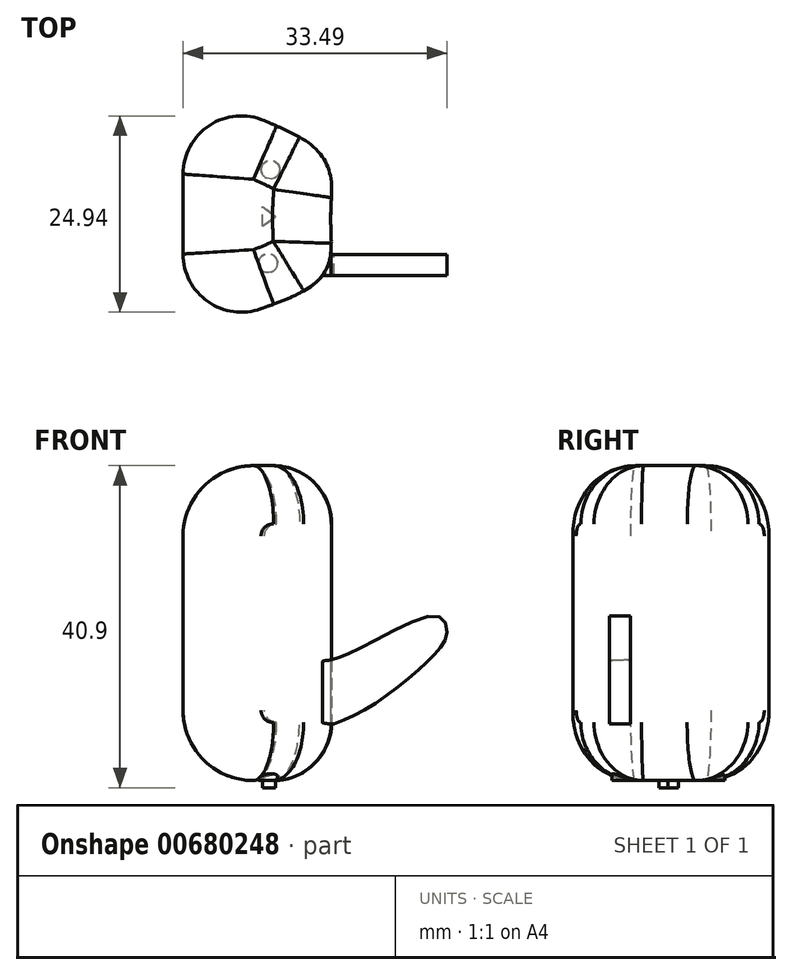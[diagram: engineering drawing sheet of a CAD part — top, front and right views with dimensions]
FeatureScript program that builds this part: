
annotation { "Feature Type Name" : "Feature", "Feature Type Description" : "" }
export const myFeature = defineFeature(function(context is Context, id is Id, definition is map)
    precondition{}
    {
        {
            var Q0;
            Q0=qCreatedBy(makeId("Top.planeOp"),FACE);
            var sketch = newSketch(context, id + "F0", { "sketchPlane" : qUnion([Q0])});
            skLineSegment(sketch, "E0", {"start": v(-0.87, 0) * mm, "end": v(-0.87, 30) * mm});
            skFitSpline(sketch, "E1", {"points": [v(-0.87, 0) * mm, v(9.33, 2.9) * mm, v(17.04, 7.3) * mm, v(17.87, 14.2) * mm, v(17.87, 19.53) * mm, v(15.67, 23.38) * mm, v(10.06, 26.42) * mm, v(4.27, 28.9) * mm, v(-0.87, 30) * mm], "startDerivative": vector(97.67, 19.37) * mm, "endDerivative": vector(-53.84, -1.92) * mm});
            skSolve(sketch);
        }
        {
            var Q0;
            Q0 = qSketchRegion(id + "F0", true);
            extrude(context, id + "F1", {"entities" : qUnion([Q0]), "depth" : 40 * mm, "offsetDistance" : 25 * mm});
        }
        {
            var Q0;
            Q0=makeQuery(id+"F1.opExtrude","CAP_EDGE",EDGE,{"disambiguationData":[OSD([sQuery(id+"F0.wireOp",EDGE,"E0")])],"isStart":false});
            fillet(context, id + "F2", {"entities" : qUnion([Q0]), "radius" : 8.93 * mm, "tangentPropagation" : true, "allowEdgeOverflow" : false});
        }
        {
            var Q0;
            Q0=makeQuery(id+"F1.opExtrude","CAP_EDGE",EDGE,{"disambiguationData":[OSD([sQuery(id+"F0.wireOp",EDGE,"E0")])],"isStart":true});
            fillet(context, id + "F3", {"entities" : qUnion([Q0]), "radius" : 8.93 * mm, "tangentPropagation" : true, "allowEdgeOverflow" : false});
        }
        {
            var Q0;
            Q0=makeQuery(id+"F1.opExtrude","CAP_EDGE",EDGE,{"disambiguationData":[OSD([sQuery(id+"F0.wireOp",EDGE,"E1")])],"isStart":true});
            var Q1;
            Q1=makeQuery(id+"F3.opFillet","BLEND_EDGE",EDGE,{"disambiguationData":[OD(1.0)],"blendedFrom":[makeQuery(id+"F1.opExtrude","CAP_EDGE",EDGE,{"disambiguationData":[OSD([sQuery(id+"F0.wireOp",EDGE,"E0")])],"isStart":true}),makeQuery(id+"F1.opExtrude","SWEPT_FACE",FACE,{"disambiguationData":[OSD([sQuery(id+"F0.wireOp",EDGE,"E1")])]})],"blendedInto":[makeQuery(id+"F1.opExtrude","SWEPT_FACE",FACE,{"disambiguationData":[OSD([sQuery(id+"F0.wireOp",EDGE,"E1")])]})]});
            var Q2;
            Q2=makeQuery(id+"F3.opFillet","BLEND_EDGE",EDGE,{"disambiguationData":[OD(0.0)],"blendedFrom":[makeQuery(id+"F1.opExtrude","CAP_EDGE",EDGE,{"disambiguationData":[OSD([sQuery(id+"F0.wireOp",EDGE,"E0")])],"isStart":true}),makeQuery(id+"F1.opExtrude","SWEPT_FACE",FACE,{"disambiguationData":[OSD([sQuery(id+"F0.wireOp",EDGE,"E1")])]})],"blendedInto":[makeQuery(id+"F1.opExtrude","SWEPT_FACE",FACE,{"disambiguationData":[OSD([sQuery(id+"F0.wireOp",EDGE,"E1")])]})]});
            fillet(context, id + "F4", {"entities" : qUnion([Q0, Q1, Q2]), "radius" : 7.39 * mm, "tangentPropagation" : true, "allowEdgeOverflow" : false});
        }
        {
            var Q0;
            Q0=qCreatedBy(makeId("Top.planeOp"),FACE);
            var sketch = newSketch(context, id + "F5", { "sketchPlane" : qUnion([Q0])});
            skCircle(sketch, "E2", {"center": v(10.23, 20.47) * mm, "radius": 1.19 * mm});
            skSolve(sketch);
        }
        {
            var Q0;
            Q0=qCreatedBy(makeId("Top.planeOp"),FACE);
            var sketch = newSketch(context, id + "F6", { "sketchPlane" : qUnion([Q0])});
            skCircle(sketch, "E3", {"center": v(9.91, 8.57) * mm, "radius": 1.21 * mm});
            skSolve(sketch);
        }
        {
            var Q0;
            Q0=qCreatedBy(makeId("Top.planeOp"),FACE);
            var sketch = newSketch(context, id + "F7", { "sketchPlane" : qUnion([Q0])});
            skLineSegment(sketch, "E4", {"start": v(10.88, 14.46) * mm, "end": v(9.2, 15.8) * mm});
            skLineSegment(sketch, "E5", {"start": v(9.2, 15.8) * mm, "end": v(9.2, 13.28) * mm});
            skLineSegment(sketch, "E6", {"start": v(9.2, 13.28) * mm, "end": v(10.88, 14.46) * mm});
            skSolve(sketch);
        }
        {
            var Q0;
            Q0=makeQuery(id+"F6.imprint","IMPRINT",FACE,{"disambiguationData":[TD([[makeQuery(id+"F6.imprint","IMPRINT",EDGE,{"derivedFrom":sQuery(id+"F6.wireOp",EDGE,"E3")}),1.0]])]});
            var Q1;
            Q1=makeQuery(id+"F5.imprint","IMPRINT",FACE,{"disambiguationData":[TD([[makeQuery(id+"F5.imprint","IMPRINT",EDGE,{"derivedFrom":sQuery(id+"F5.wireOp",EDGE,"E2")}),1.0]])]});
            extrude(context, id + "F8", {"entities" : qUnion([Q0, Q1]), "operationType" : NewBodyOperationType.ADD, "endBound" : BoundingType.UP_TO_NEXT, "depth" : 25 * mm, "offsetDistance" : 25 * mm});
        }
        {
            var Q0;
            Q0=qCreatedBy(makeId("Front.planeOp"),FACE);
            cPlane(context, id + "F9", {"entities" : qUnion([Q0]), "cplaneType" : CPlaneType.OFFSET, "offset" : 9.7 * mm, "oppositeDirection" : true, "width" : 150 * mm, "height" : 150 * mm});
        }
        {
            var Q0;
            Q0=makeQuery(id+"F7.imprint","IMPRINT",FACE,{"disambiguationData":[TD([[makeQuery(id+"F7.imprint","IMPRINT",EDGE,{"derivedFrom":sQuery(id+"F7.wireOp",EDGE,"E4")}),1.0]])]});
            extrude(context, id + "F10", {"entities" : qUnion([Q0]), "operationType" : NewBodyOperationType.ADD, "endBound" : BoundingType.UP_TO_NEXT, "depth" : 25 * mm, "offsetDistance" : 25 * mm, "hasSecondDirection" : true, "secondDirectionOppositeDirection" : true, "secondDirectionDepth" : 0.9 * mm});
        }
        {
            var Q0;
            Q0=qCreatedBy(id+"F9.planeOp",FACE);
            var sketch = newSketch(context, id + "F11", { "sketchPlane" : qUnion([Q0])});
            skFitSpline(sketch, "E7", {"points": [v(18.32, 7.22) * mm, v(22.37, 9.11) * mm, v(27.84, 13.06) * mm, v(31.37, 16.36) * mm, v(32.57, 18.46) * mm, v(31.62, 20.84) * mm, v(21.66, 16.83) * mm, v(17.93, 15.3) * mm], "startDerivative": vector(28.37, 11.47) * mm, "endDerivative": vector(-22.27, -7) * mm});
            skArc(sketch, "E8", {"start": v(17.93, 15.3) * mm, "mid": v(13.85, 11.05) * mm, "end": v(18.32, 7.22) * mm});
            skSolve(sketch);
        }
        {
            var Q0;
            Q0=makeQuery(id+"F11.imprint","IMPRINT",FACE,{"disambiguationData":[TD([[makeQuery(id+"F11.imprint","IMPRINT",EDGE,{"derivedFrom":sQuery(id+"F11.wireOp",EDGE,"E7")}),1.0]])]});
            extrude(context, id + "F12", {"entities" : qUnion([Q0]), "operationType" : NewBodyOperationType.ADD, "depth" : 2.7 * mm, "offsetDistance" : 25 * mm});
        }
        {
            var Q0;
            Q0=qCreatedBy(id+"F9.planeOp",FACE);
            cPlane(context, id + "F13", {"entities" : qUnion([Q0]), "cplaneType" : CPlaneType.OFFSET, "offset" : 5 * mm, "oppositeDirection" : true, "width" : 150 * mm, "height" : 150 * mm});
        }
    });
